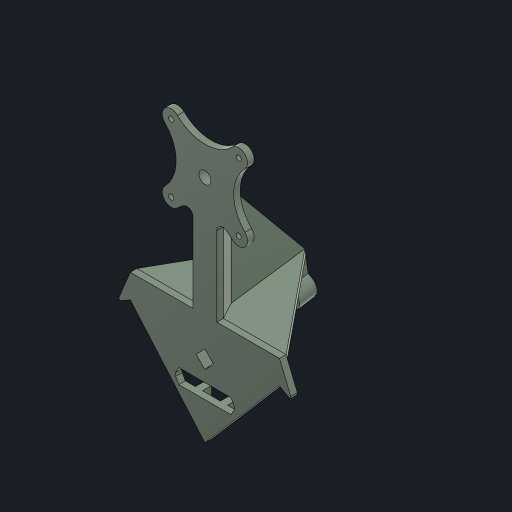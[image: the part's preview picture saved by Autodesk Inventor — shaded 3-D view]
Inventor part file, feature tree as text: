
AUTODESK INVENTOR PART (.ipt)
format: ipt  version: 2023 (Build 270158000, 158)  size: 446,464 bytes
history: native  units: mm
features: extrude x16, sketch x14, other x6, fillet x4, projected_geometry x3, chamfer x2, mirror x1, hole x1
ambient origin geometry x8: Origin, YZ Plane, XZ Plane, XY Plane, X Axis, Y Axis, Z Axis, Center Point
bodies: Body1 (feature_tree)
feature tree (47):
  other  "ソリッド1"
  sketch  "スケッチ1"
  extrude  "押し出し1"  Depth=2.2mm
  extrude  "押し出し2"  Depth=40.0mm
  extrude  "押し出し4"  Depth=14.3117mm
  extrude  "押し出し5"  Depth=8.0mm
  extrude  "爪"  Depth=180.0mm
  extrude  "押し出し17"  Depth=15.0mm
  extrude  "押し出し20"  Depth=14.0499mm
  extrude  "押し出し21"  Depth=30.0mm
  mirror  "ミラー1"
  extrude  "モーター土台"  Depth=25.0mm TaperAngle=0.0deg
  hole  "穴1"  [1 undecoded]
  other  "作業平面2"
  extrude  "押し出し10"  Depth=1.6mm TaperAngle=0.0deg
  extrude  "ロッド穴"  TaperAngle=0.0deg  [1 undecoded]
  extrude  "押し出し12"  Depth=3.0mm
  extrude  "押し出し13"  Depth=35.0mm
  other  "作業平面3"
  extrude  "押し出し11"  Depth=1.4mm TaperAngle=0.0deg
  fillet  "フィレット2"  Radius=1.0mm
  other  "YZ平面"
  other  "XZ平面"
  extrude  "押し出し22"  Depth=4.2mm
  fillet  "フィレット3"  [1 undecoded]
  fillet  "フィレット4"  Radius=8.0mm
  extrude  "押し出し23"  Depth=5.0mm TaperAngle=0.0deg
  fillet  "フィレット5"  Radius=6.0mm
  chamfer  "面取り1"  Distance=6.0mm
  chamfer  "面取り2"  Distance=3.0mm
  sketch  "スケッチ2"
  sketch  "スケッチ3"
  other  "作業平面1"
  sketch  "スケッチ6"
  sketch  "スケッチ7"
  sketch  "スケッチ8"
  projected_geometry  "投影ループ1"
  sketch  "スケッチ9"
  sketch  "スケッチ11"
  sketch  "スケッチ15"
  sketch  "スケッチ16"
  sketch  "スケッチ21"
  sketch  "スケッチ22"
  projected_geometry  "投影ループ2"
  sketch  "スケッチ23"
  sketch  "スケッチ24"
  projected_geometry  "投影ループ3"
note: 3 required parameter values undecoded (feature->parameter linkage not recoverable at this tier; creation-order binding heuristic only, values carry confidence <= 0.55)
